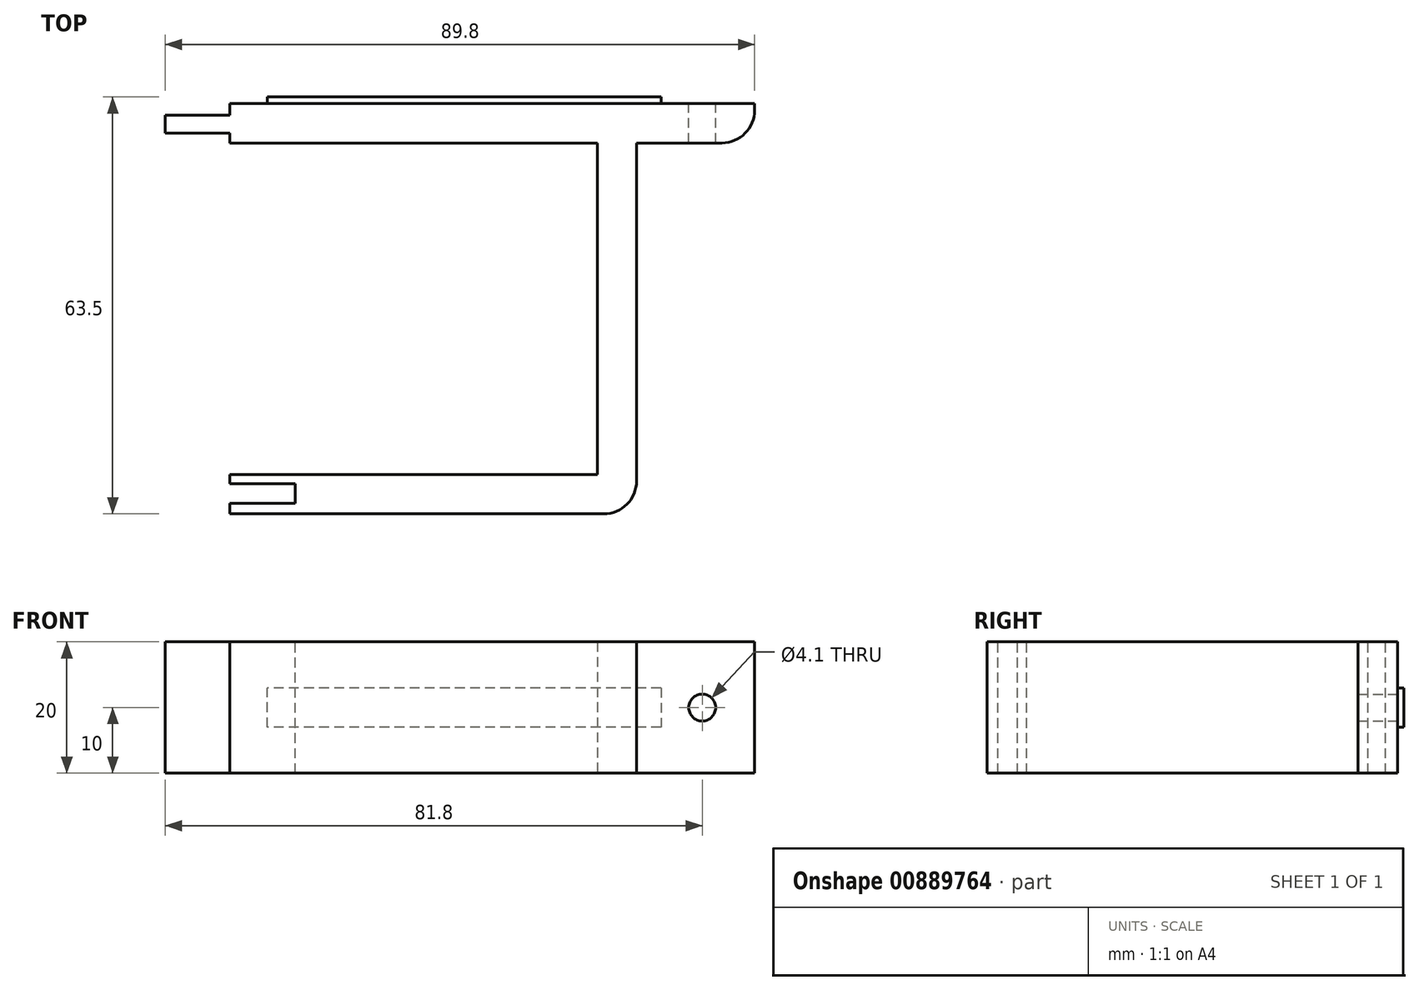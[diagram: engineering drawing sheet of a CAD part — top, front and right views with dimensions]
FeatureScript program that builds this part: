
annotation { "Feature Type Name" : "Feature", "Feature Type Description" : "" }
export const myFeature = defineFeature(function(context is Context, id is Id, definition is map)
    precondition{}
    {
        {
            var Q0;
            Q0=qCreatedBy(makeId("Top.planeOp"),FACE);
            var sketch = newSketch(context, id + "F0", { "sketchPlane" : qUnion([Q0])});
            skLineSegment(sketch, "E0.bottom", {"start": v(-80, 3) * mm, "end": v(80, 3) * mm});
            skLineSegment(sketch, "E0.top", {"start": v(-80, -3) * mm, "end": v(-62, -3) * mm});
            skLineSegment(sketch, "E0.left", {"start": v(-80, 3) * mm, "end": v(-80, -3) * mm});
            skLineSegment(sketch, "E0.right", {"start": v(80, 3) * mm, "end": v(80, -3) * mm});
            skPoint(sketch, "E0.middle", {"position": v(0, 0) * mm});
            skLineSegment(sketch, "E1.bottom", {"start": v(-56, -3) * mm, "end": v(56, -3) * mm});
            skLineSegment(sketch, "E1.top", {"start": v(-56, -53.5) * mm, "end": v(56, -53.5) * mm});
            skLineSegment(sketch, "E1.left", {"start": v(-56, -3) * mm, "end": v(-56, -53.5) * mm});
            skLineSegment(sketch, "E1.right", {"start": v(56, -3) * mm, "end": v(56, -53.5) * mm});
            skLineSegment(sketch, "E2", {"start": v(-62, -3) * mm, "end": v(-62, -59.5) * mm});
            skLineSegment(sketch, "E3", {"start": v(-62, -59.5) * mm, "end": v(62, -59.5) * mm});
            skLineSegment(sketch, "E4", {"start": v(62, -59.5) * mm, "end": v(62, -3) * mm});
            skLineSegment(sketch, "E5.trimOffspring", {"start": v(62, -3) * mm, "end": v(80, -3) * mm});
            skSolve(sketch);
        }
        {
            var Q0;
            Q0=makeQuery(id+"F0.imprint","IMPRINT",FACE,{"disambiguationData":[TD([[makeQuery(id+"F0.imprint","IMPRINT",EDGE,{"derivedFrom":sQuery(id+"F0.wireOp",EDGE,"E0.bottom")}),-1.0]])]});
            extrude(context, id + "F1", {"entities" : qUnion([Q0]), "depth" : 20 * mm, "offsetDistance" : 25 * mm});
        }
        {
            var Q0;
            Q0=makeQuery(id+"F1.opExtrude","SWEPT_EDGE",EDGE,{"disambiguationData":[OSD([sQuery(id+"F0.wireOp",EDGE,"E3"),sQuery(id+"F0.wireOp",EDGE,"E4")])]});
            var Q1;
            Q1=makeQuery(id+"F1.opExtrude","SWEPT_EDGE",EDGE,{"disambiguationData":[OSD([sQuery(id+"F0.wireOp",EDGE,"E2"),sQuery(id+"F0.wireOp",EDGE,"E3")])]});
            var Q2;
            Q2=makeQuery(id+"F1.opExtrude","SWEPT_EDGE",EDGE,{"disambiguationData":[OSD([sQuery(id+"F0.wireOp",EDGE,"E0.top"),sQuery(id+"F0.wireOp",EDGE,"E0.left")])]});
            var Q3;
            Q3=makeQuery(id+"F1.opExtrude","SWEPT_EDGE",EDGE,{"disambiguationData":[OSD([sQuery(id+"F0.wireOp",EDGE,"E0.right"),sQuery(id+"F0.wireOp",EDGE,"E5.trimOffspring")])]});
            fillet(context, id + "F2", {"entities" : qUnion([Q0, Q1, Q2, Q3]), "radius" : 5 * mm, "tangentPropagation" : true, "allowEdgeOverflow" : false});
        }
        {
            var Q0;
            Q0=makeQuery(id+"F1.opExtrude","SWEPT_FACE",FACE,{"disambiguationData":[OSD([sQuery(id+"F0.wireOp",EDGE,"E0.bottom")])]});
            var sketch = newSketch(context, id + "F3", { "sketchPlane" : qUnion([Q0])});
            skPoint(sketch, "E6", {"position": v(-72, 10) * mm});
            skPoint(sketch, "E7", {"position": v(72, 10) * mm});
            skSolve(sketch);
        }
        {
            var Q0;
            Q0=sQuery(id+"F3.wireOp",VERTEX,"E6");
            var Q1;
            Q1=sQuery(id+"F3.wireOp",VERTEX,"E7");
            var Q2;
            Q2=makeQuery(id+"F1.opExtrude","SWEPT_BODY",BODY,{"disambiguationData":[OSD([sQuery(id+"F0.wireOp",EDGE,"E0.bottom"),sQuery(id+"F0.wireOp",EDGE,"E0.top"),sQuery(id+"F0.wireOp",EDGE,"E0.left"),sQuery(id+"F0.wireOp",EDGE,"E0.right"),sQuery(id+"F0.wireOp",EDGE,"E1.top"),sQuery(id+"F0.wireOp",EDGE,"E1.left"),sQuery(id+"F0.wireOp",EDGE,"E1.right"),sQuery(id+"F0.wireOp",EDGE,"E2"),sQuery(id+"F0.wireOp",EDGE,"E3"),sQuery(id+"F0.wireOp",EDGE,"E4"),sQuery(id+"F0.wireOp",EDGE,"E5.trimOffspring"),sQuery(id+"F0.wireOp",EDGE,"E1.bottom")])]});
            hole(context, id + "F4", {"style" : HoleStyle.SIMPLE, "endStyle" : HoleEndStyle.THROUGH, "holeDiameter" : 4.1 * mm, "majorDiameter" : 5 * mm, "isTappedThrough" : true, "tappedDepth" : 12 * mm, "tapClearance" : 3, "locations" : qUnion([Q0, Q1]), "scope" : qUnion([Q2])});
        }
        {
            var Q0;
            Q0=makeQuery(id+"F1.opExtrude","CAP_FACE",FACE,{"disambiguationData":[OSD([sQuery(id+"F0.wireOp",EDGE,"E0.bottom"),sQuery(id+"F0.wireOp",EDGE,"E0.top"),sQuery(id+"F0.wireOp",EDGE,"E0.left"),sQuery(id+"F0.wireOp",EDGE,"E0.right"),sQuery(id+"F0.wireOp",EDGE,"E1.top"),sQuery(id+"F0.wireOp",EDGE,"E1.left"),sQuery(id+"F0.wireOp",EDGE,"E1.right"),sQuery(id+"F0.wireOp",EDGE,"E2"),sQuery(id+"F0.wireOp",EDGE,"E3"),sQuery(id+"F0.wireOp",EDGE,"E4"),sQuery(id+"F0.wireOp",EDGE,"E5.trimOffspring"),sQuery(id+"F0.wireOp",EDGE,"E1.bottom")])],"isStart":false});
            var sketch = newSketch(context, id + "F5", { "sketchPlane" : qUnion([Q0])});
            skLineSegment(sketch, "E8.bottom", {"start": v(10, -54.88) * mm, "end": v(0, -54.88) * mm});
            skLineSegment(sketch, "E8.top", {"start": v(10, -57.88) * mm, "end": v(0, -57.88) * mm});
            skLineSegment(sketch, "E8.left", {"start": v(10, -54.88) * mm, "end": v(10, -57.88) * mm});
            skPoint(sketch, "E8.middle.positionSnap0", {"position": v(0, -53.5) * mm});
            skPoint(sketch, "E8.centerSnap0", {"position": v(0, -53.5) * mm});
            skLineSegment(sketch, "E9.bottom", {"start": v(0, 1.2) * mm, "end": v(-9.8, 1.2) * mm});
            skLineSegment(sketch, "E9.top", {"start": v(0, -1.5) * mm, "end": v(-9.8, -1.5) * mm});
            skLineSegment(sketch, "E9.right", {"start": v(-9.8, 1.2) * mm, "end": v(-9.8, -1.5) * mm});
            skPoint(sketch, "E9.middle", {"position": v(0, 0) * mm});
            skLineSegment(sketch, "E10", {"start": v(0, -54.88) * mm, "end": v(0, -53.5) * mm});
            skLineSegment(sketch, "E11", {"start": v(0, -57.88) * mm, "end": v(0, -59.5) * mm});
            skLineSegment(sketch, "E12", {"start": v(0, -3) * mm, "end": v(0, -1.5) * mm});
            skLineSegment(sketch, "E13", {"start": v(0, 3) * mm, "end": v(0, 1.2) * mm});
            skSolve(sketch);
        }
        {
            var Q0;
            Q0=makeQuery(id+"F5.imprint","IMPRINT",FACE,{"disambiguationData":[TD([[makeQuery(id+"F5.imprint","IMPRINT",EDGE,{"derivedFrom":sQuery(id+"F5.wireOp",EDGE,"E8.bottom")}),1.0]])]});
            extrude(context, id + "F6", {"entities" : qUnion([Q0]), "operationType" : NewBodyOperationType.REMOVE, "endBound" : BoundingType.UP_TO_NEXT, "oppositeDirection" : true, "depth" : 25 * mm, "offsetDistance" : 25 * mm});
        }
        {
            var Q0;
            Q0=makeQuery(id+"F1.opExtrude","SWEPT_FACE",FACE,{"disambiguationData":[OSD([sQuery(id+"F0.wireOp",EDGE,"E0.bottom")])]});
            var sketch = newSketch(context, id + "F7", { "sketchPlane" : qUnion([Q0])});
            skLineSegment(sketch, "E14.bottom", {"start": v(-65.73, 13) * mm, "end": v(-5.73, 13) * mm});
            skLineSegment(sketch, "E14.top", {"start": v(-65.73, 7) * mm, "end": v(-5.73, 7) * mm});
            skLineSegment(sketch, "E14.left", {"start": v(-65.73, 13) * mm, "end": v(-65.73, 7) * mm});
            skPoint(sketch, "E14.middle", {"position": v(0, 10) * mm});
            skLineSegment(sketch, "E15", {"start": v(-5.73, 7) * mm, "end": v(-5.73, 13) * mm});
            skPoint(sketch, "E14.right.end.orphan", {"position": v(65.73, 7) * mm});
            skPoint(sketch, "E14.right.start.orphan", {"position": v(65.73, 13) * mm});
            skSolve(sketch);
        }
        {
            var Q0;
            Q0=makeQuery(id+"F7.imprint","IMPRINT",FACE,{"disambiguationData":[TD([[makeQuery(id+"F7.imprint","IMPRINT",EDGE,{"derivedFrom":sQuery(id+"F7.wireOp",EDGE,"E14.bottom")}),-1.0]])]});
            extrude(context, id + "F8", {"entities" : qUnion([Q0]), "operationType" : NewBodyOperationType.ADD, "depth" : 1 * mm, "offsetDistance" : 25 * mm});
        }
    });
